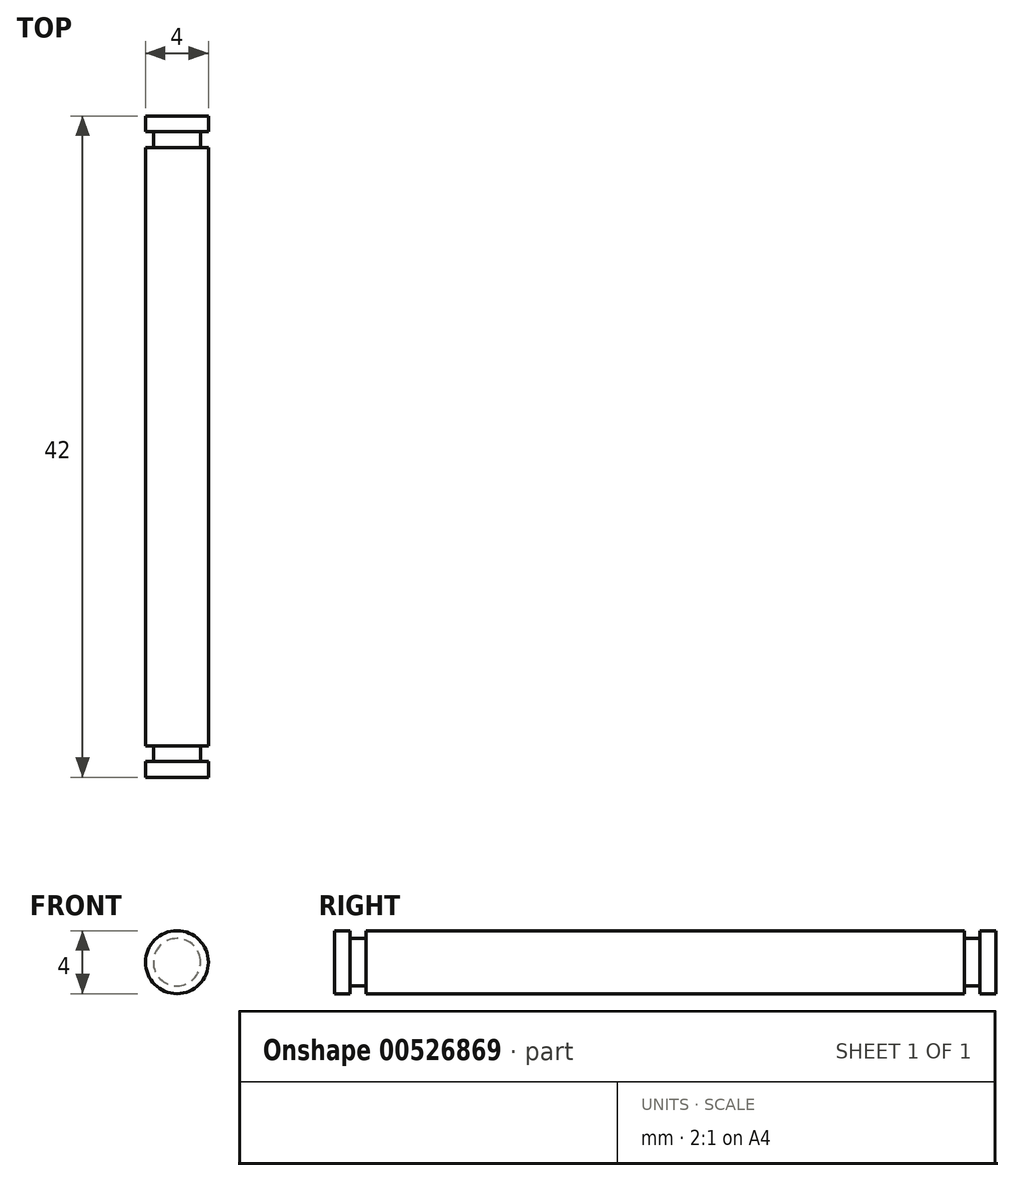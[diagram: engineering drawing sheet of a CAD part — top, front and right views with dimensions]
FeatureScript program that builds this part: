
annotation { "Feature Type Name" : "Feature", "Feature Type Description" : "" }
export const myFeature = defineFeature(function(context is Context, id is Id, definition is map)
    precondition{}
    {
        {
            var Q0;
            Q0=qCreatedBy(makeId("Front.planeOp"),FACE);
            var sketch = newSketch(context, id + "F0", { "sketchPlane" : qUnion([Q0])});
            skCircle(sketch, "E0", {"center": v(0, 0) * mm, "radius": 2 * mm});
            skSolve(sketch);
        }
        {
            var Q0;
            Q0=makeQuery(id+"F0.imprint","IMPRINT",FACE,{"disambiguationData":[TD([[makeQuery(id+"F0.imprint","IMPRINT",EDGE,{"derivedFrom":sQuery(id+"F0.wireOp",EDGE,"E0")}),1.0]])]});
            extrude(context, id + "F1", {"entities" : qUnion([Q0]), "depth" : 42 * mm, "offsetDistance" : 25 * mm});
        }
        {
            var Q0;
            Q0=qCreatedBy(makeId("Right.planeOp"),FACE);
            var sketch = newSketch(context, id + "F2", { "sketchPlane" : qUnion([Q0])});
            skLineSegment(sketch, "E1.bottom", {"start": v(-41, 6.03) * mm, "end": v(-40, 6.03) * mm});
            skLineSegment(sketch, "E1.top", {"start": v(-41, 1.5) * mm, "end": v(-40, 1.5) * mm});
            skLineSegment(sketch, "E1.left", {"start": v(-40, 6.03) * mm, "end": v(-40, 1.5) * mm});
            skLineSegment(sketch, "E1.right", {"start": v(-41, 6.03) * mm, "end": v(-41, 1.5) * mm});
            skLineSegment(sketch, "E2.bottom", {"start": v(-2, 7.12) * mm, "end": v(-1, 7.12) * mm});
            skLineSegment(sketch, "E2.top", {"start": v(-2, 1.5) * mm, "end": v(-1, 1.5) * mm});
            skLineSegment(sketch, "E2.left", {"start": v(-2, 7.12) * mm, "end": v(-2, 1.5) * mm});
            skLineSegment(sketch, "E2.right", {"start": v(-1, 7.12) * mm, "end": v(-1, 1.5) * mm});
            skSolve(sketch);
        }
        {
            var Q0;
            Q0=makeQuery(id+"F2.imprint","IMPRINT",FACE,{"disambiguationData":[TD([[makeQuery(id+"F2.imprint","IMPRINT",EDGE,{"derivedFrom":sQuery(id+"F2.wireOp",EDGE,"E1.bottom")}),-1.0]])]});
            var Q1;
            Q1=makeQuery(id+"F2.imprint","IMPRINT",FACE,{"disambiguationData":[TD([[makeQuery(id+"F2.imprint","IMPRINT",EDGE,{"derivedFrom":sQuery(id+"F2.wireOp",EDGE,"E2.bottom")}),-1.0]])]});
            var Q2;
            Q2=makeQuery(id+"F1.opExtrude","SWEPT_FACE",FACE,{"disambiguationData":[OSD([sQuery(id+"F0.wireOp",EDGE,"E0")])]});
            revolve(context, id + "F3", {"operationType" : NewBodyOperationType.REMOVE, "entities" : qUnion([Q0, Q1]), "axis" : qUnion([Q2]), "revolveType" : RevolveType.FULL, "oppositeDirection" : true});
        }
    });
